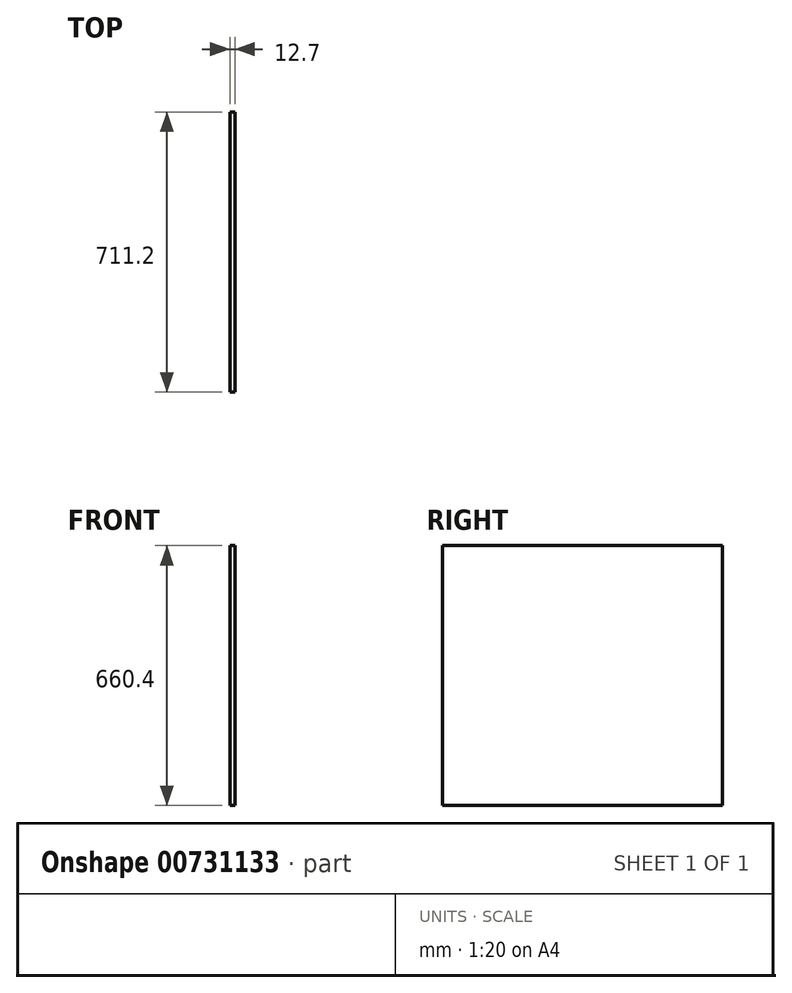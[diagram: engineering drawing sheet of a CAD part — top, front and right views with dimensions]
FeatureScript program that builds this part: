
annotation { "Feature Type Name" : "Feature", "Feature Type Description" : "" }
export const myFeature = defineFeature(function(context is Context, id is Id, definition is map)
    precondition{}
    {
        {
            var Q0;
            Q0=qCreatedBy(makeId("Right.planeOp"),FACE);
            var sketch = newSketch(context, id + "F0", { "sketchPlane" : qUnion([Q0])});
            skLineSegment(sketch, "E0.bottom", {"start": v(355.6, 330.2) * mm, "end": v(-355.6, 330.2) * mm});
            skLineSegment(sketch, "E0.top", {"start": v(355.6, -330.2) * mm, "end": v(-355.6, -330.2) * mm});
            skLineSegment(sketch, "E0.left", {"start": v(355.6, 330.2) * mm, "end": v(355.6, -330.2) * mm});
            skLineSegment(sketch, "E0.right", {"start": v(-355.6, 330.2) * mm, "end": v(-355.6, -330.2) * mm});
            skPoint(sketch, "E0.middle", {"position": v(0, 0) * mm});
            skSolve(sketch);
        }
        {
            var Q0;
            Q0 = qSketchRegion(id + "F0", true);
            extrude(context, id + "F1", {"entities" : qUnion([Q0]), "depth" : 12.7 * mm, "offsetDistance" : 25.4 * mm});
        }
    });
